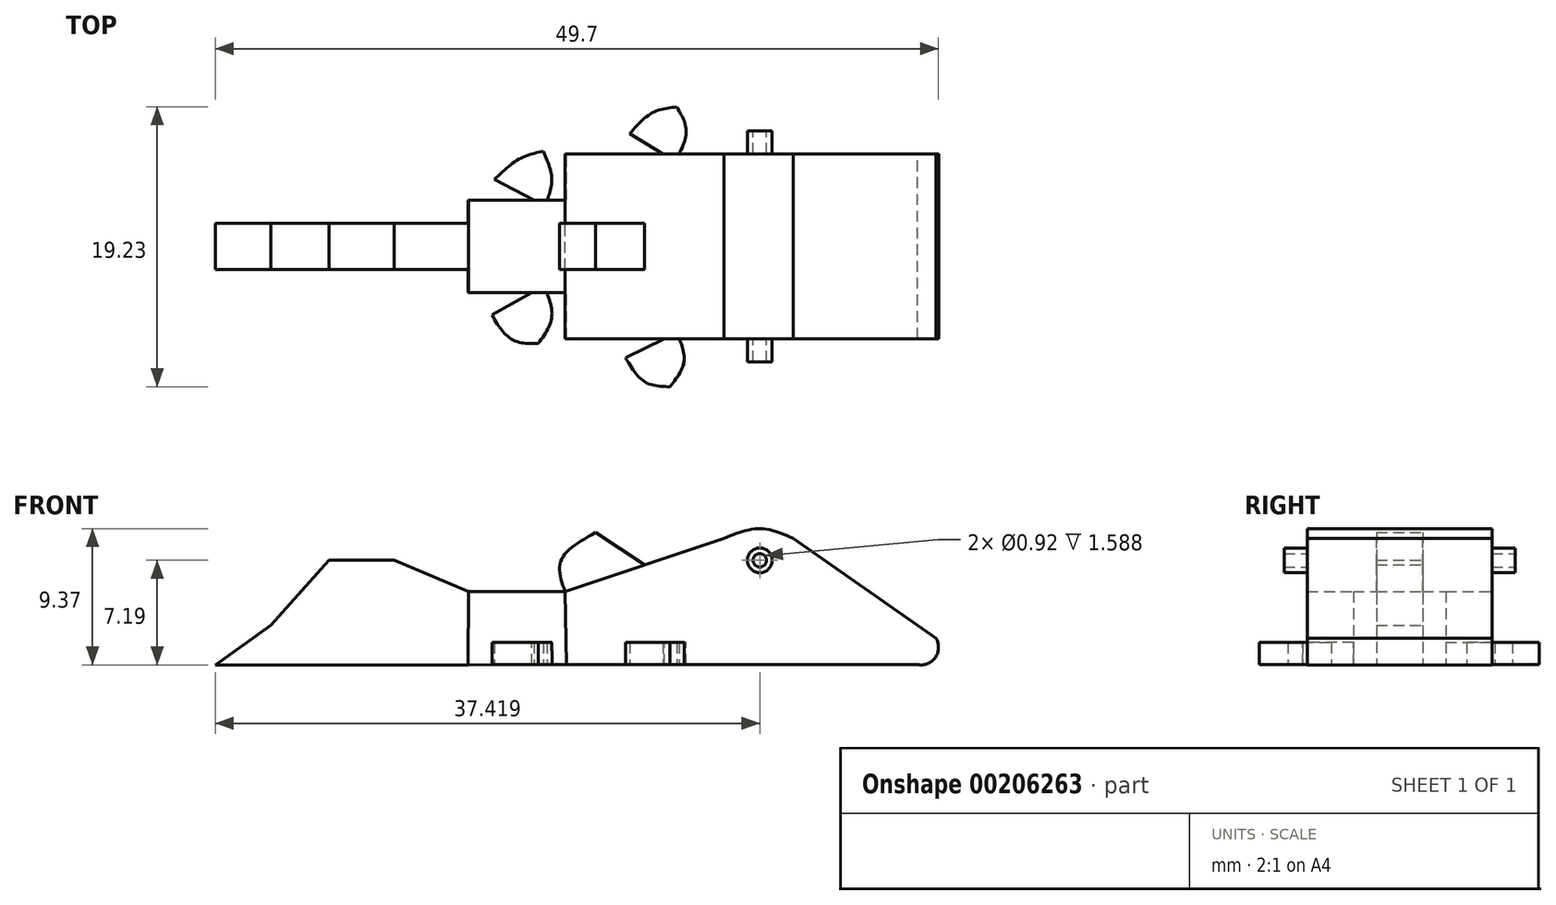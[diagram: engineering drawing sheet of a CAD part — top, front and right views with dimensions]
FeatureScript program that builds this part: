
annotation { "Feature Type Name" : "Feature", "Feature Type Description" : "" }
export const myFeature = defineFeature(function(context is Context, id is Id, definition is map)
    precondition{}
    {
        {
            var Q0;
            Q0=qCreatedBy(makeId("Front.planeOp"),FACE);
            var sketch = newSketch(context, id + "F0", { "sketchPlane" : qUnion([Q0])});
            skArc(sketch, "E0", {"start": v(27.87, -7.16) * mm, "mid": v(29.1, -6.67) * mm, "end": v(29.15, -5.36) * mm});
            skLineSegment(sketch, "E1", {"start": v(29.15, -5.36) * mm, "end": v(19.31, 1.52) * mm});
            skFitSpline(sketch, "E2", {"points": [v(19.31, 1.52) * mm, v(17.03, 2.18) * mm, v(14.57, 1.52) * mm], "startDerivative": vector(-4.6, 2) * mm, "endDerivative": vector(-4.88, -1.97) * mm});
            skLineSegment(sketch, "E3", {"start": v(14.57, 1.52) * mm, "end": v(3.64, -2.15) * mm});
            skLineSegment(sketch, "E4", {"start": v(3.64, -2.15) * mm, "end": v(-3, -2.15) * mm});
            skLineSegment(sketch, "E5", {"start": v(-3, -2.15) * mm, "end": v(-8.1, 0) * mm});
            skLineSegment(sketch, "E6", {"start": v(-8.1, 0) * mm, "end": v(-12.59, 0) * mm});
            skLineSegment(sketch, "E7", {"start": v(-12.59, 0) * mm, "end": v(-16.58, -4.46) * mm});
            skLineSegment(sketch, "E8", {"start": v(-16.58, -4.46) * mm, "end": v(-20.4, -7.19) * mm});
            skLineSegment(sketch, "E9", {"start": v(9.1, -0.32) * mm, "end": v(5.74, 1.9) * mm});
            skFitSpline(sketch, "E10", {"points": [v(5.74, 1.9) * mm, v(3.37, 0) * mm, v(3.64, -2.15) * mm], "startDerivative": vector(-5.72, -3.19) * mm, "endDerivative": vector(1.73, -4.98) * mm});
            skCircle(sketch, "E11", {"center": v(17.03, 0) * mm, "radius": 0.85 * mm});
            skCircle(sketch, "E12", {"center": v(17.03, 0) * mm, "radius": 0.46 * mm});
            skLineSegment(sketch, "E13", {"start": v(-3, -2.15) * mm, "end": v(-3, -7.19) * mm});
            skLineSegment(sketch, "E14", {"start": v(-20.4, -7.19) * mm, "end": v(27.87, -7.16) * mm});
            skLineSegment(sketch, "E15", {"start": v(3.64, -2.15) * mm, "end": v(3.74, -7.18) * mm});
            skSolve(sketch);
        }
        {
            var Q0;
            {var subQ3=sQuery(id+"F0.wireOp",EDGE,"E0");Q0=makeQuery(id+"F0.imprint","IMPRINT",FACE,{"disambiguationData":[TD([[makeQuery(id+"F0.imprint","IMPRINT",EDGE,{"derivedFrom":subQ3}),1.0]])]});}
            extrude(context, id + "F1", {"entities" : qUnion([Q0]), "endBound" : BoundingType.SYMMETRIC, "depth" : 12.7 * mm});
        }
        {
            var Q0;
            {var subQ0=sQuery(id+"F0.wireOp",EDGE,"E4");Q0=makeQuery(id+"F0.imprint","IMPRINT",FACE,{"disambiguationData":[TD([[makeQuery(id+"F0.imprint","IMPRINT",EDGE,{"derivedFrom":subQ0}),1.0]])]});}
            extrude(context, id + "F2", {"entities" : qUnion([Q0]), "operationType" : NewBodyOperationType.ADD, "endBound" : BoundingType.SYMMETRIC, "depth" : 6.35 * mm});
        }
        {
            var Q0;
            {var subQ2=sQuery(id+"F0.wireOp",EDGE,"E5");Q0=makeQuery(id+"F0.imprint","IMPRINT",FACE,{"disambiguationData":[TD([[makeQuery(id+"F0.imprint","IMPRINT",EDGE,{"derivedFrom":subQ2}),1.0]])]});}
            extrude(context, id + "F3", {"entities" : qUnion([Q0]), "operationType" : NewBodyOperationType.ADD, "endBound" : BoundingType.SYMMETRIC, "depth" : 3.17 * mm});
        }
        {
            var Q0;
            {var subQ2=sQuery(id+"F0.wireOp",EDGE,"E9");Q0=makeQuery(id+"F0.imprint","IMPRINT",FACE,{"disambiguationData":[TD([[makeQuery(id+"F0.imprint","IMPRINT",EDGE,{"derivedFrom":subQ2}),1.0]])]});}
            extrude(context, id + "F4", {"entities" : qUnion([Q0]), "operationType" : NewBodyOperationType.ADD, "endBound" : BoundingType.SYMMETRIC, "depth" : 3.17 * mm});
        }
        {
            var Q0;
            Q0=makeQuery(id+"F0.imprint","IMPRINT",FACE,{"disambiguationData":[TD([[makeQuery(id+"F0.imprint","IMPRINT",EDGE,{"derivedFrom":sQuery(id+"F0.wireOp",EDGE,"E11")}),1.0]])]});
            extrude(context, id + "F5", {"entities" : qUnion([Q0]), "operationType" : NewBodyOperationType.ADD, "endBound" : BoundingType.SYMMETRIC, "depth" : 15.88 * mm});
        }
        {
            var Q0;
            Q0=makeQuery(id+"F0.imprint","IMPRINT",FACE,{"disambiguationData":[TD([[makeQuery(id+"F0.imprint","IMPRINT",EDGE,{"derivedFrom":sQuery(id+"F0.wireOp",EDGE,"E12")}),1.0]])]});
            extrude(context, id + "F6", {"entities" : qUnion([Q0]), "operationType" : NewBodyOperationType.ADD, "endBound" : BoundingType.SYMMETRIC, "depth" : 12.7 * mm});
        }
        {
            var Q0;
            {var subQ0=sQuery(id+"F0.wireOp",EDGE,"E14");Q0=makeQuery(id+"F3.boolean.opBoolean","MERGE",FACE,{"derivedFrom":[makeQuery(id+"F2.boolean.opBoolean","MERGE",FACE,{"derivedFrom":[makeQuery(id+"F1.opExtrude","SWEPT_FACE",FACE,{"disambiguationData":[OSD([subQ0])]}),makeQuery(id+"F2.opExtrude","SWEPT_FACE",FACE,{"disambiguationData":[OSD([subQ0])]})]}),makeQuery(id+"F3.opExtrude","SWEPT_FACE",FACE,{"disambiguationData":[OSD([subQ0])]})]});}
            cPlane(context, id + "F7", {"entities" : qUnion([Q0]), "cplaneType" : CPlaneType.OFFSET, "offset" : 0 * mm, "width" : 152.4 * mm, "height" : 152.4 * mm});
        }
        {
            var Q0;
            Q0=qCreatedBy(id+"F7.planeOp",FACE);
            var sketch = newSketch(context, id + "F8", { "sketchPlane" : qUnion([Q0])});
            skFitSpline(sketch, "E16", {"points": [v(11.47, 6.29) * mm, v(11.82, 7.95) * mm, v(10.86, 9.64) * mm], "startDerivative": vector(1.33, 3.49) * mm, "endDerivative": vector(-2.52, 3.23) * mm});
            skFitSpline(sketch, "E17", {"points": [v(2.37, 3.14) * mm, v(2.72, 4.94) * mm, v(1.8, 6.67) * mm], "startDerivative": vector(1.32, 3.74) * mm, "endDerivative": vector(-2.46, 3.33) * mm});
            skLineSegment(sketch, "E18", {"start": v(10.57, 6.3) * mm, "end": v(7.81, 7.66) * mm});
            skLineSegment(sketch, "E19", {"start": v(1.35, 3.17) * mm, "end": v(-1.39, 4.7) * mm});
            skFitSpline(sketch, "E20", {"points": [v(10.86, 9.64) * mm, v(9.14, 9.31) * mm, v(7.81, 7.66) * mm], "startDerivative": vector(-3.86, -0.11) * mm, "endDerivative": vector(-2.26, -3.8) * mm});
            skFitSpline(sketch, "E21", {"points": [v(1.8, 6.67) * mm, v(0, 6.4) * mm, v(-1.39, 4.7) * mm], "startDerivative": vector(-4.03, 0.08) * mm, "endDerivative": vector(-2.36, -3.93) * mm});
            skFitSpline(sketch, "E22", {"points": [v(11.45, -6.26) * mm, v(11.97, -7.98) * mm, v(11.31, -9.59) * mm], "startDerivative": vector(1.63, -3.46) * mm, "endDerivative": vector(-1.9, -3.2) * mm});
            skFitSpline(sketch, "E23", {"points": [v(2.4, -3.14) * mm, v(2.73, -4.66) * mm, v(2.14, -6.55) * mm], "startDerivative": vector(1.12, -3.17) * mm, "endDerivative": vector(-1.59, -3.65) * mm});
            skLineSegment(sketch, "E24", {"start": v(10.57, -6.23) * mm, "end": v(8.09, -7.75) * mm});
            skLineSegment(sketch, "E25", {"start": v(1.57, -3.14) * mm, "end": v(-1.22, -4.61) * mm});
            skFitSpline(sketch, "E26", {"points": [v(11.31, -9.59) * mm, v(9.63, -9.17) * mm, v(8.09, -7.75) * mm], "startDerivative": vector(-3.68, 0.42) * mm, "endDerivative": vector(-2.79, 3.2) * mm});
            skFitSpline(sketch, "E27", {"points": [v(2.14, -6.55) * mm, v(0.5, -6) * mm, v(-1.22, -4.61) * mm], "startDerivative": vector(-3.56, 0.82) * mm, "endDerivative": vector(-3.16, 3.01) * mm});
            skLineSegment(sketch, "E28", {"start": v(10.57, -6.23) * mm, "end": v(11.45, -6.26) * mm});
            skLineSegment(sketch, "E29", {"start": v(1.57, -3.14) * mm, "end": v(2.4, -3.14) * mm});
            skLineSegment(sketch, "E30", {"start": v(1.35, 3.17) * mm, "end": v(2.37, 3.14) * mm});
            skLineSegment(sketch, "E31", {"start": v(10.57, 6.3) * mm, "end": v(11.47, 6.29) * mm});
            skSolve(sketch);
        }
        {
            var Q0;
            Q0=makeQuery(id+"F8.imprint","IMPRINT",FACE,{"disambiguationData":[TD([[makeQuery(id+"F8.imprint","IMPRINT",EDGE,{"derivedFrom":sQuery(id+"F8.wireOp",EDGE,"E16")}),1.0]])]});
            var Q1;
            Q1=makeQuery(id+"F8.imprint","IMPRINT",FACE,{"disambiguationData":[TD([[makeQuery(id+"F8.imprint","IMPRINT",EDGE,{"derivedFrom":sQuery(id+"F8.wireOp",EDGE,"E22")}),-1.0]])]});
            var Q2;
            Q2=makeQuery(id+"F8.imprint","IMPRINT",FACE,{"disambiguationData":[TD([[makeQuery(id+"F8.imprint","IMPRINT",EDGE,{"derivedFrom":sQuery(id+"F8.wireOp",EDGE,"E23")}),-1.0]])]});
            var Q3;
            Q3=makeQuery(id+"F8.imprint","IMPRINT",FACE,{"disambiguationData":[TD([[makeQuery(id+"F8.imprint","IMPRINT",EDGE,{"derivedFrom":sQuery(id+"F8.wireOp",EDGE,"E17")}),1.0]])]});
            extrude(context, id + "F9", {"entities" : qUnion([Q0, Q1, Q2, Q3]), "operationType" : NewBodyOperationType.ADD, "oppositeDirection" : true, "depth" : 1.52 * mm});
        }
    });
